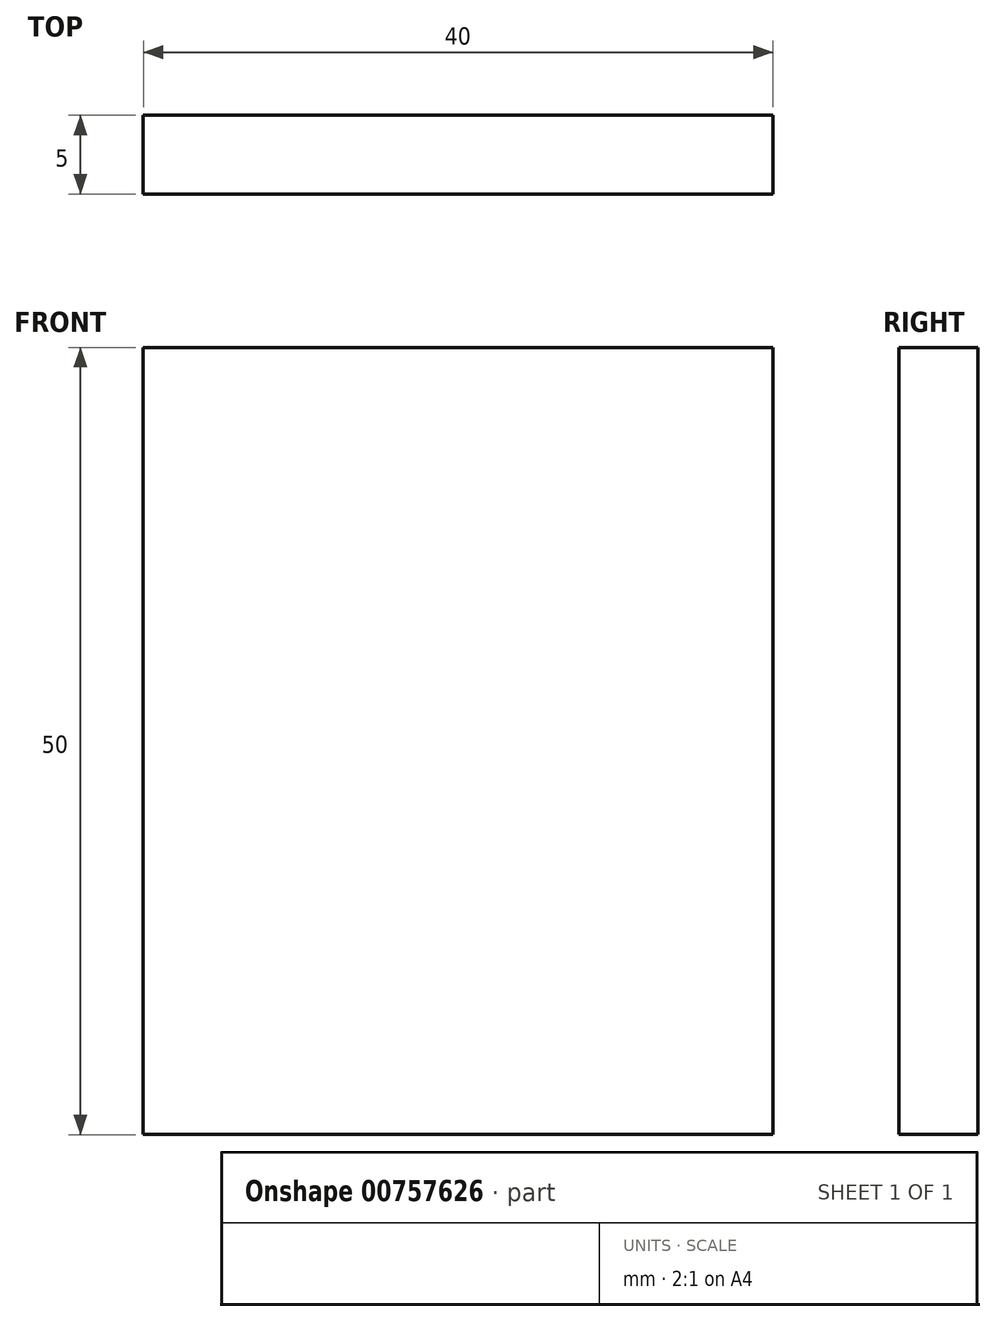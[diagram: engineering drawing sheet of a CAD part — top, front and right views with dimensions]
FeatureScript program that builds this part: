
annotation { "Feature Type Name" : "Feature", "Feature Type Description" : "" }
export const myFeature = defineFeature(function(context is Context, id is Id, definition is map)
    precondition{}
    {
        {
            var Q0;
            Q0=qCreatedBy(makeId("Front.planeOp"),FACE);
            var sketch = newSketch(context, id + "F0", { "sketchPlane" : qUnion([Q0])});
            skLineSegment(sketch, "E0.bottom", {"start": v(-17.6, 11.35) * mm, "end": v(22.4, 11.35) * mm});
            skLineSegment(sketch, "E0.top", {"start": v(-17.6, -38.65) * mm, "end": v(22.4, -38.65) * mm});
            skLineSegment(sketch, "E0.left", {"start": v(-17.6, 11.35) * mm, "end": v(-17.6, -38.65) * mm});
            skLineSegment(sketch, "E0.right", {"start": v(22.4, 11.35) * mm, "end": v(22.4, -38.65) * mm});
            skSolve(sketch);
        }
        {
            var Q0;
            Q0 = qSketchRegion(id + "F0", true);
            extrude(context, id + "F1", {"entities" : qUnion([Q0]), "depth" : 5 * mm, "offsetDistance" : 25 * mm});
        }
    });
